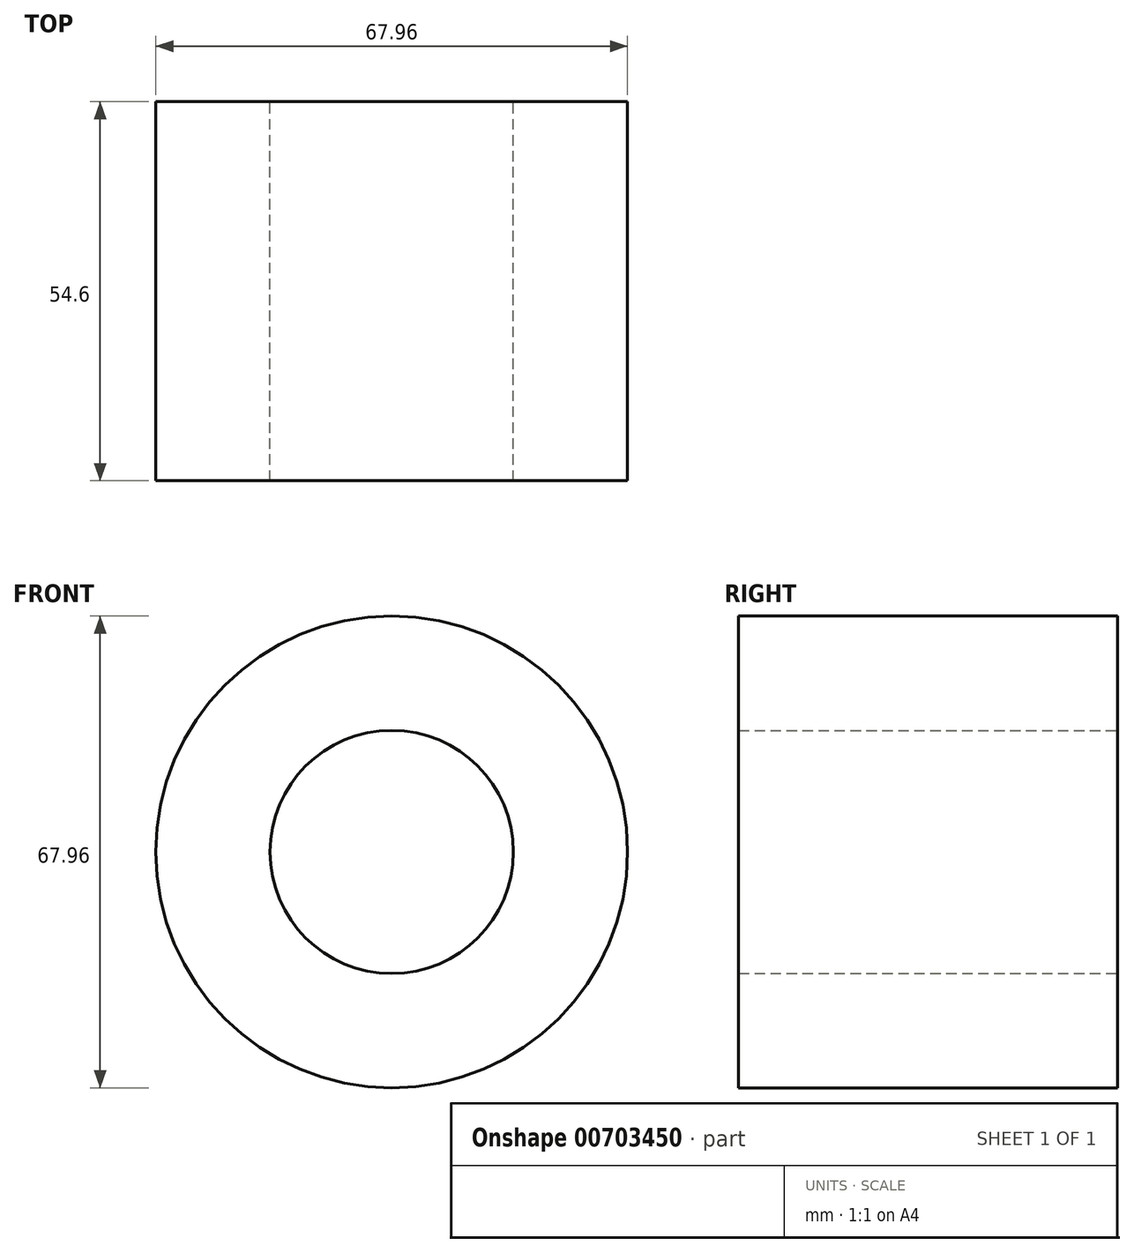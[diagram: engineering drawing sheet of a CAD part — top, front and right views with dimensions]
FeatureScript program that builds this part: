
annotation { "Feature Type Name" : "Feature", "Feature Type Description" : "" }
export const myFeature = defineFeature(function(context is Context, id is Id, definition is map)
    precondition{}
    {
        {
            var Q0;
            Q0=qCreatedBy(makeId("Front.planeOp"),FACE);
            var sketch = newSketch(context, id + "F0", { "sketchPlane" : qUnion([Q0])});
            skCircle(sketch, "E0", {"center": v(0, 0) * mm, "radius": 33.98 * mm});
            skCircle(sketch, "E1", {"center": v(0, 0) * mm, "radius": 17.52 * mm});
            skSolve(sketch);
        }
        {
            var Q0;
            Q0=makeQuery(id+"F0.imprint","IMPRINT",FACE,{"disambiguationData":[TD([[makeQuery(id+"F0.imprint","IMPRINT",EDGE,{"derivedFrom":sQuery(id+"F0.wireOp",EDGE,"E0")}),1.0]])]});
            extrude(context, id + "F1", {"entities" : qUnion([Q0]), "depth" : 54.6 * mm, "offsetDistance" : 25 * mm});
        }
    });
